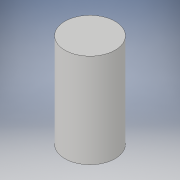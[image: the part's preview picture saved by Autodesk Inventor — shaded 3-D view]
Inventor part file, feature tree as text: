
AUTODESK INVENTOR PART (.ipt)
format: ipt  version: 2019 (Build 230136000, 136)  size: 91,136 bytes
history: native  units: mm
features: revolve x1, sketch x1
ambient origin geometry x8: Origin, YZ Plane, XZ Plane, XY Plane, X Axis, Y Axis, Z Axis, Center Point
bodies: Solid1 (feature_tree)
feature tree (2):
  revolve  "Revolution1"  [1 undecoded]
  sketch  "Sketch1"  dims[d0=8.0mm d1=15.0mm d2=90.0deg]
note: 1 required parameter value undecoded (feature->parameter linkage not recoverable at this tier; creation-order binding heuristic only, values carry confidence <= 0.55)
